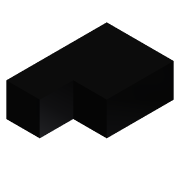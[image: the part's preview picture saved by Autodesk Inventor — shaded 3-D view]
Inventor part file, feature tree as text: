
AUTODESK INVENTOR PART (.ipt)
format: ipt  version: 2015 (Build 190159000, 159)  size: 76,800 bytes
history: native  units: in
note: dims shown in document units (in); Inventor stores cm internally (conversion verified against a paired STEP export)
features: extrude x1, sketch x1
ambient origin geometry x8: Origin, YZ Plane, XZ Plane, XY Plane, X Axis, Y Axis, Z Axis, Center Point
bodies: Solid1 (feature_tree)
feature tree (2):
  extrude  "Extrusion1"  Depth=2.0in
  sketch  "Sketch1"  dims[d0=3.0in d1=2.0in d2=2.0in d3=1.0in d4=1.0in d5=0.0in]
